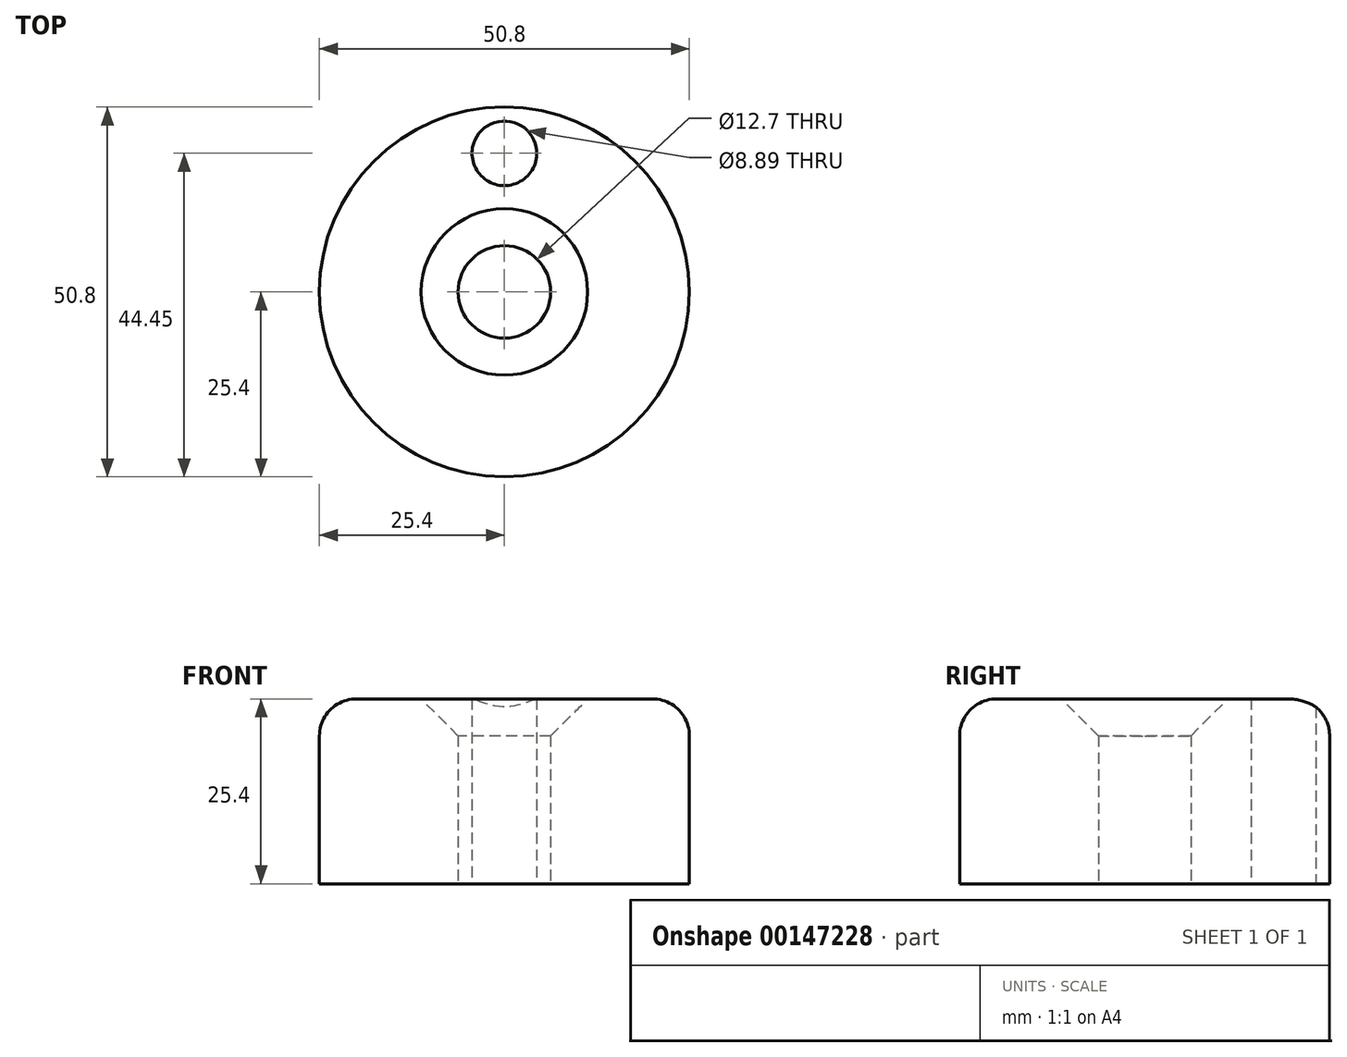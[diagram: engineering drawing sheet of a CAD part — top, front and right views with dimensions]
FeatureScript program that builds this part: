
annotation { "Feature Type Name" : "Feature", "Feature Type Description" : "" }
export const myFeature = defineFeature(function(context is Context, id is Id, definition is map)
    precondition{}
    {
        {
            var Q0;
            Q0=qCreatedBy(makeId("Top.planeOp"),FACE);
            var sketch = newSketch(context, id + "F0", { "sketchPlane" : qUnion([Q0])});
            skCircle(sketch, "E0", {"center": v(0, 0) * mm, "radius": 25.4 * mm});
            skCircle(sketch, "E1", {"center": v(0, 0) * mm, "radius": 6.35 * mm});
            skCircle(sketch, "E2", {"center": v(0, 19.05) * mm, "radius": 4.45 * mm});
            skSolve(sketch);
        }
        {
            var Q0;
            Q0=makeQuery(id+"F0.imprint","IMPRINT",FACE,{"disambiguationData":[TD([[makeQuery(id+"F0.imprint","IMPRINT",EDGE,{"derivedFrom":sQuery(id+"F0.wireOp",EDGE,"E0")}),1.0]])]});
            extrude(context, id + "F1", {"entities" : qUnion([Q0]), "depth" : 25.4 * mm});
        }
        {
            var Q0;
            Q0=makeQuery(id+"F1.opExtrude","CAP_EDGE",EDGE,{"disambiguationData":[OSD([sQuery(id+"F0.wireOp",EDGE,"E0")])],"isStart":false});
            fillet(context, id + "F2", {"entities" : qUnion([Q0]), "radius" : 5.08 * mm, "tangentPropagation" : true, "allowEdgeOverflow" : false});
        }
        {
            var Q0;
            Q0=makeQuery(id+"F1.opExtrude","CAP_EDGE",EDGE,{"disambiguationData":[OSD([sQuery(id+"F0.wireOp",EDGE,"E1")])],"isStart":false});
            chamfer(context, id + "F3", {"entities" : qUnion([Q0]), "width" : 5.08 * mm, "tangentPropagation" : true});
        }
    });
